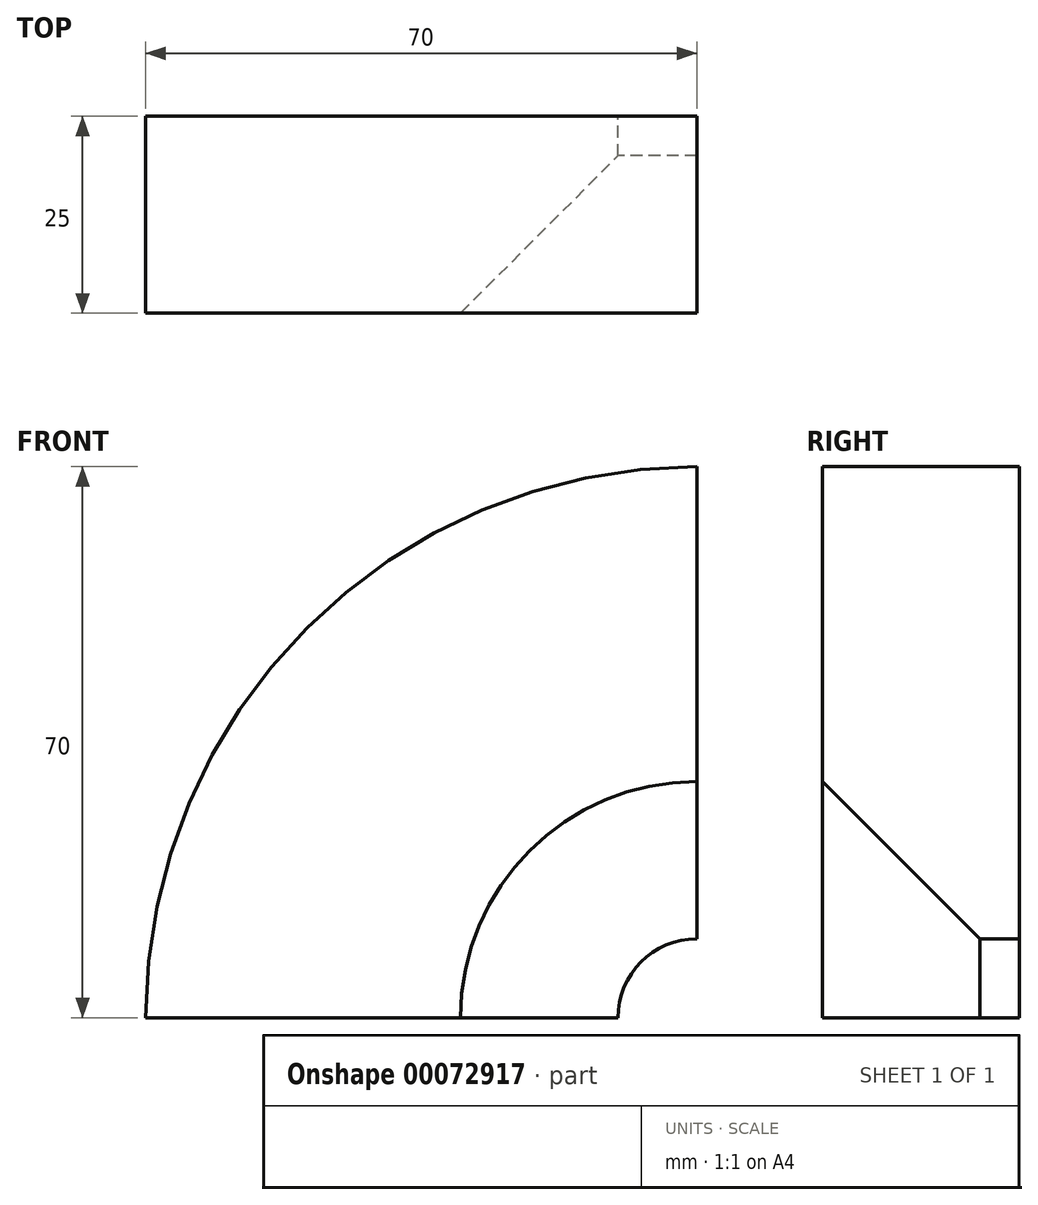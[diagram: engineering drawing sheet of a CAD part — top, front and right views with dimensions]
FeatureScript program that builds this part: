
annotation { "Feature Type Name" : "Feature", "Feature Type Description" : "" }
export const myFeature = defineFeature(function(context is Context, id is Id, definition is map)
    precondition{}
    {
        {
            var Q0;
            Q0=qCreatedBy(makeId("Front.planeOp"),FACE);
            var sketch = newSketch(context, id + "F0", { "sketchPlane" : qUnion([Q0])});
            skArc(sketch, "E0", {"start": v(0, 70) * mm, "mid": v(-49.5, 49.5) * mm, "end": v(-70, 0) * mm});
            skArc(sketch, "E1", {"start": v(-10, 0) * mm, "mid": v(-7.07, 7.07) * mm, "end": v(0, 10) * mm});
            skLineSegment(sketch, "E2", {"start": v(0, 70) * mm, "end": v(0, 10) * mm});
            skLineSegment(sketch, "E3", {"start": v(-10, 0) * mm, "end": v(-70, 0) * mm});
            skArc(sketch, "E4", {"start": v(-40.66, 29.1) * mm, "mid": v(-47.6, 15.28) * mm, "end": v(-50, 0) * mm, "construction": true});
            skCircle(sketch, "E5", {"center": v(0, 0) * mm, "radius": 70 * mm, "construction": true});
            skSolve(sketch);
        }
        {
            var Q0;
            Q0 = qSketchRegion(id + "F0", true);
            extrude(context, id + "F1", {"entities" : qUnion([Q0]), "depth" : 25 * mm});
        }
        {
            var Q0;
            Q0=makeQuery(id+"F1.opExtrude","CAP_EDGE",EDGE,{"disambiguationData":[OSD([sQuery(id+"F0.wireOp",EDGE,"E1")])],"isStart":false});
            chamfer(context, id + "F2", {"entities" : qUnion([Q0]), "width" : 20 * mm, "tangentPropagation" : true});
        }
    });
